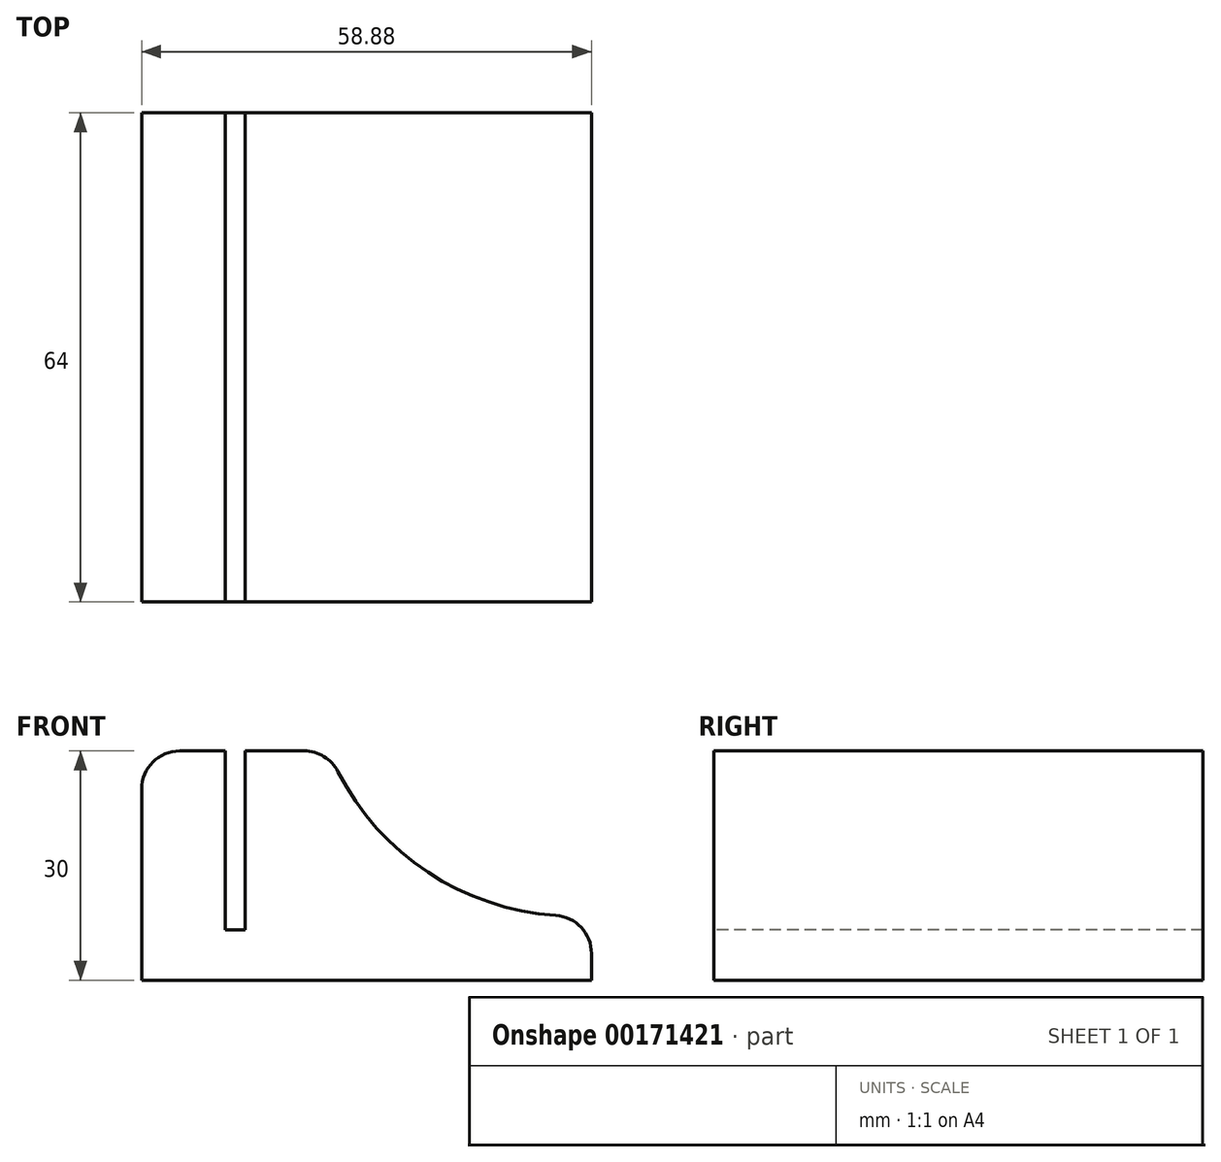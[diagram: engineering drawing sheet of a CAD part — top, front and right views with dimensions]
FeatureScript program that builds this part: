
annotation { "Feature Type Name" : "Feature", "Feature Type Description" : "" }
export const myFeature = defineFeature(function(context is Context, id is Id, definition is map)
    precondition{}
    {
        {
            var Q0;
            Q0=qCreatedBy(makeId("Front.planeOp"),FACE);
            var sketch = newSketch(context, id + "F0", { "sketchPlane" : qUnion([Q0])});
            skLineSegment(sketch, "E0", {"start": v(0, -5.2) * mm, "end": v(0, -35.2) * mm});
            skLineSegment(sketch, "E1", {"start": v(0, -5.2) * mm, "end": v(24.45, -5.2) * mm});
            skLineSegment(sketch, "E2", {"start": v(0, -35.2) * mm, "end": v(58.88, -35.2) * mm});
            skLineSegment(sketch, "E3", {"start": v(58.88, -35.2) * mm, "end": v(58.88, -26.72) * mm});
            skArc(sketch, "E4", {"start": v(24.45, -5.2) * mm, "mid": v(38.18, -21.54) * mm, "end": v(58.88, -26.72) * mm});
            skSolve(sketch);
        }
        {
            var Q0;
            Q0=makeQuery(id+"F0.imprint","IMPRINT",FACE,{"disambiguationData":[TD([[makeQuery(id+"F0.imprint","IMPRINT",EDGE,{"derivedFrom":sQuery(id+"F0.wireOp",EDGE,"E0")}),1.0]])]});
            extrude(context, id + "F1", {"entities" : qUnion([Q0]), "depth" : 64 * mm});
        }
        {
            var Q0;
            Q0=makeQuery(id+"F1.opExtrude","SWEPT_FACE",FACE,{"disambiguationData":[OSD([sQuery(id+"F0.wireOp",EDGE,"E1")])]});
            var sketch = newSketch(context, id + "F2", { "sketchPlane" : qUnion([Q0])});
            skLineSegment(sketch, "E5", {"start": v(12.23, -64) * mm, "end": v(12.23, 0) * mm, "construction": true});
            skLineSegment(sketch, "E6", {"start": v(0, -32) * mm, "end": v(0, -32) * mm});
            skLineSegment(sketch, "E7.bottom", {"start": v(10.93, 0) * mm, "end": v(13.53, 0) * mm});
            skLineSegment(sketch, "E7.top", {"start": v(10.93, -64) * mm, "end": v(13.53, -64) * mm});
            skLineSegment(sketch, "E7.left", {"start": v(10.93, 0) * mm, "end": v(10.93, -64) * mm});
            skLineSegment(sketch, "E7.right", {"start": v(13.53, 0) * mm, "end": v(13.53, -64) * mm});
            skPoint(sketch, "E7.middle", {"position": v(12.23, -32) * mm});
            skSolve(sketch);
        }
        {
            var Q0;
            Q0=makeQuery(id+"F2.imprint","IMPRINT",FACE,{"disambiguationData":[TD([[makeQuery(id+"F2.imprint","IMPRINT",EDGE,{"derivedFrom":sQuery(id+"F2.wireOp",EDGE,"E7.bottom")}),-1.0]])]});
            extrude(context, id + "F3", {"entities" : qUnion([Q0]), "operationType" : NewBodyOperationType.REMOVE, "oppositeDirection" : true, "depth" : 23.4 * mm});
        }
        {
            var Q0;
            Q0=makeQuery(id+"F1.opExtrude","SWEPT_EDGE",EDGE,{"disambiguationData":[OSD([sQuery(id+"F0.wireOp",EDGE,"E1"),sQuery(id+"F0.wireOp",EDGE,"E4")])]});
            var Q1;
            Q1=makeQuery(id+"F1.opExtrude","SWEPT_EDGE",EDGE,{"disambiguationData":[OSD([sQuery(id+"F0.wireOp",EDGE,"E0"),sQuery(id+"F0.wireOp",EDGE,"E1")])]});
            var Q2;
            Q2=makeQuery(id+"F1.opExtrude","SWEPT_EDGE",EDGE,{"disambiguationData":[OSD([sQuery(id+"F0.wireOp",EDGE,"E3"),sQuery(id+"F0.wireOp",EDGE,"E4")])]});
            fillet(context, id + "F4", {"entities" : qUnion([Q0, Q1, Q2]), "radius" : 5 * mm, "tangentPropagation" : true, "allowEdgeOverflow" : false});
        }
    });
